# Revit family: 1
name_source: partatom
category: Furniture
revit_build: Autodesk Revit 2017 (Build: 20160225_1515(x64)
units: mm (PartAtom-declared; Revit-internal decimal feet)

## family parameters
Always vertical = Yes
Cut with Voids When Loaded = No
OmniClass Number = 23.40.20.00
OmniClass Title = General Furniture and Specialties
Room Calculation Point = No
Shared = No
Work Plane-Based = No

## types (30) — shared parameters
Assembly Code = E2020200
D = 980 mm  [stored 3.21522 ft]
H = 1215 mm  [stored 3.98622 ft]
Keynote = 12490
Kind = Sofa
Leg = okm_G155
Manufacturer = Okamura Corporation
Product Categories = NAGARE
URL = http://www.okamura.co.jp
W = 750 mm  [stored 2.46063 ft]

## per-type parameters (varying)
| type | Armrest_2D | Armrest_3D | Body | Common Specification | Product Number |
| Armless_F30A(Shell) | No | No | okm_F30A | Armless | 4LNABA |
| Armless_F31A(Clay) | No | No | okm_F31A | Armless | 4LNABA |
| Armless_F32A(Cafe) | No | No | okm_F32A | Armless | 4LNABA |
| Armless_F33A(Charcoal) | No | No | okm_F33A | Armless | 4LNABA |
| Armless_F34A(Ink) | No | No | okm_F34A | Armless | 4LNABA |
| Armless_F35A(Ice) | No | No | okm_F35A | Armless | 4LNABA |
| Armless_F36A(Peacock) | No | No | okm_F36A | Armless | 4LNABA |
| Armless_F37A(Cactus) | No | No | okm_F37A | Armless | 4LNABA |
| Armless_F38A(Soil) | No | No | okm_F38A | Armless | 4LNABA |
| Armless_F39A(Aloe) | No | No | okm_F39A | Armless | 4LNABA |
| Armless_F40A(Sunset) | No | No | okm_F40A | Armless | 4LNABA |
| Armless_F41A(Tango) | No | No | okm_F41A | Armless | 4LNABA |
| Armless_F42A(Rumba) | No | No | okm_F42A | Armless | 4LNABA |
| Armless_F43A(Fig) | No | No | okm_F43A | Armless | 4LNABA |
| Armless_F44A(Coral) | No | No | okm_F44A | Armless | 4LNABA |
| With Armrest_F31A(Clay) | Yes | Yes | okm_F31A | With Armrest | 4LNABD |
| With Armrest_F32A(Cafe) | Yes | Yes | okm_F32A | With Armrest | 4LNABD |
| With Armrest_F33A(Charcoal) | Yes | Yes | okm_F33A | With Armrest | 4LNABD |
| With Armrest_F34A(Ink) | Yes | Yes | okm_F34A | With Armrest | 4LNABD |
| With Armrest_F35A(Ice) | Yes | Yes | okm_F35A | With Armrest | 4LNABD |
| With Armrest_F36A(Peacock) | Yes | Yes | okm_F36A | With Armrest | 4LNABD |
| With Armrest_F37A(Cactus) | Yes | Yes | okm_F37A | With Armrest | 4LNABD |
| With Armrest_F38A(Soil) | Yes | Yes | okm_F38A | With Armrest | 4LNABD |
| With Armrest_F39A(Aloe) | Yes | Yes | okm_F39A | With Armrest | 4LNABD |
| With Armrest_F40A(Sunset) | Yes | Yes | okm_F40A | With Armrest | 4LNABD |
| With Armrest_F41A(Tango) | Yes | Yes | okm_F41A | With Armrest | 4LNABD |
| With Armrest_F42A(Rumba) | Yes | Yes | okm_F42A | With Armrest | 4LNABD |
| With Armrest_F43A(Fig) | Yes | Yes | okm_F43A | With Armrest | 4LNABD |
| With Armrest_F44A(Coral) | Yes | Yes | okm_F44A | With Armrest | 4LNABD |
| With Armrest_F30A(Shell) | Yes | Yes | okm_F30A | With Armrest | 4LNABD |

note: [stored X ft] marks values corroborated as IEEE doubles in the binary element streams (Revit-internal decimal feet)
